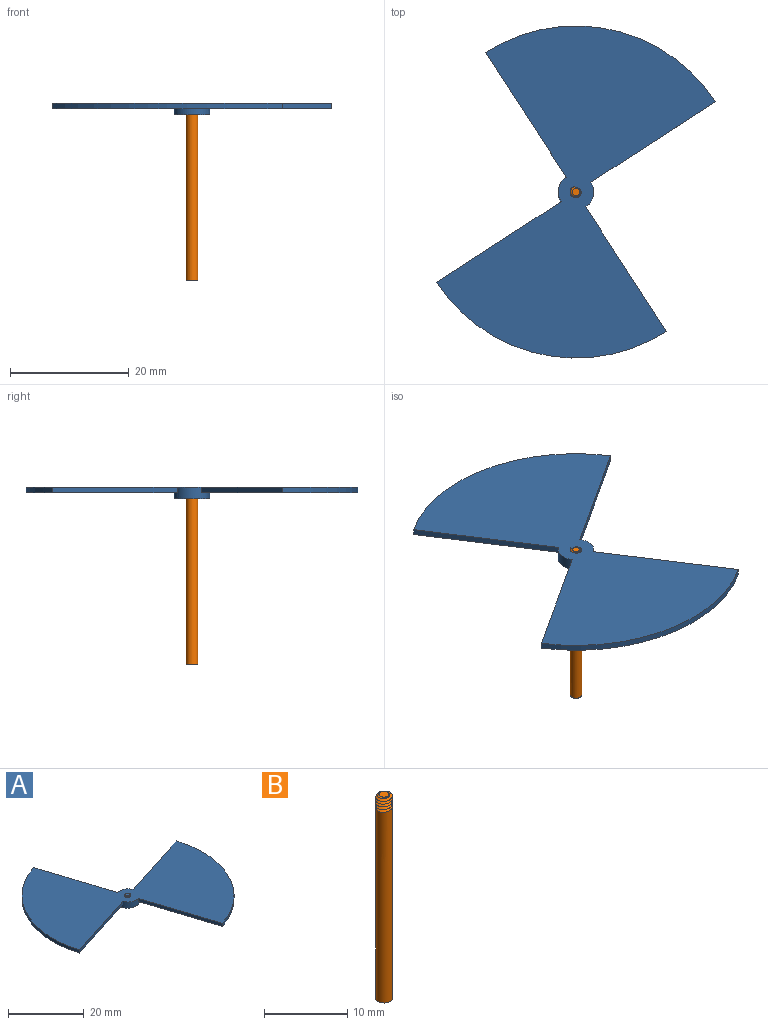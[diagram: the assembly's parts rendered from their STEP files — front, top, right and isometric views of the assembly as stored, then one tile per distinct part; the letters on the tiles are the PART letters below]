
ASSEMBLY  parts=2 mates=1
PART A: 16 faces, bbox 56.3x53.6x2.7 mm
  f0: plane 6.26x6.26mm, normal (0,0,-1), area 25.6mm2, adj f2,f3,f6,f12
  f1: plane 56.26x53.56mm, normal (0,0,1), area 1243mm2, adj f4,f5,f6,f8,f9,f10,f11,f12
  f2: plane 0.34x0.2mm, normal (0,-1,0), area 0mm2, adj f0,f5,f6
  f3: bspline ~2.31x2.2mm, area 9.7mm2, adj f0,f4,f5,f6
  f4: plane 0.34x0.2mm, normal (0,1,0), area 0mm2, adj f1,f3,f6
  f5: bspline ~2.31x2.2mm, area 9.7mm2, adj f1,f2,f3,f6
  f6: cylinder r=1mm len=2mm, axis (0,0,-1), area 0.9mm2, adj f0,f1,f2,f3,f4,f5
  f7: plane 35.24x27.08mm, normal (0,0,-1), area 608.7mm2, adj f8,f12,f13,f14
  f8: plane 23.8x7.67mm, normal (-0.31,0.95,0), area 25mm2, adj f1,f7,f12,f14
  f9: plane 23.8x7.67mm, normal (0.95,0.31,0), area 25mm2, adj f1,f10,f12,f15
  f10: cylinder r=28mm len=35.24mm, axis (0,0,-1), area 44mm2, adj f1,f9,f11,f15
  f11: plane 23.8x7.67mm, normal (0.31,-0.95,0), area 25mm2, adj f1,f10,f12,f15
  f12: cylinder r=3mm len=6mm, axis (0,0,-1), area 28.3mm2, adj f0,f1,f7,f8,f9,f11,f13,f15
  f13: plane 23.8x7.67mm, normal (-0.95,-0.31,0), area 25mm2, adj f1,f7,f12,f14
  f14: cylinder r=28mm len=35.24mm, axis (0,0,-1), area 44mm2, adj f1,f7,f8,f13
  f15: plane 35.24x27.08mm, normal (0,0,-1), area 608.7mm2, adj f9,f10,f11,f12
PART B: 12 faces, bbox 2.3x2.6x30.5 mm
  f0: cylinder r=1mm len=2mm, axis (0,0,1), area 0.1mm2, adj f1,f6,f8,f9
  f1: cylinder r=1mm len=2mm, axis (0,0,1), area 0.1mm2, adj f0,f2,f8,f9
  f2: cylinder r=1mm len=2mm, axis (0,0,1), area 0.1mm2, adj f1,f3,f8,f9
  f3: cylinder r=1mm len=2mm, axis (0,0,1), area 0.1mm2, adj f2,f4,f8,f9
  f4: cylinder r=1mm len=28.21mm, axis (0,0,1), area 176.3mm2, adj f3,f7,f8,f10,f11
  f5: plane 1.22x1.22mm, normal (0,0,1), area 1.2mm2, adj f6
  f6: cone r=0.61mm half-angle=60deg, axis (0,0,-1), area 1.2mm2, adj f0,f5,f8,f9
  f7: plane 0.34x0.2mm, normal (0,1,0), area 0mm2, adj f4,f9,f10
  f8: bspline ~2.31x2.2mm, area 9.5mm2, adj f0,f1,f2,f3,f4,f6,f9,f10
  f9: bspline ~2.31x2.2mm, area 9mm2, adj f0,f1,f2,f3,f6,f7,f8
  f10: plane 2.26x1.26mm, normal (0,0,1), area 0.5mm2, adj f4,f7,f8
  f11: plane 2x2mm, normal (0,0,-1), area 3.1mm2, adj f4
PLACE A rot(axis=(0,0,1),105.1deg) t=(70.76,-10.07,0.08)mm
PLACE B rot(axis=(0,0,1),105.1deg) t=(70.76,-10.07,1.08)mm
MATE fastened A.f6 <-> B.f0  axis (0,0,1) through (70.76,-10.07,1.08)mm
